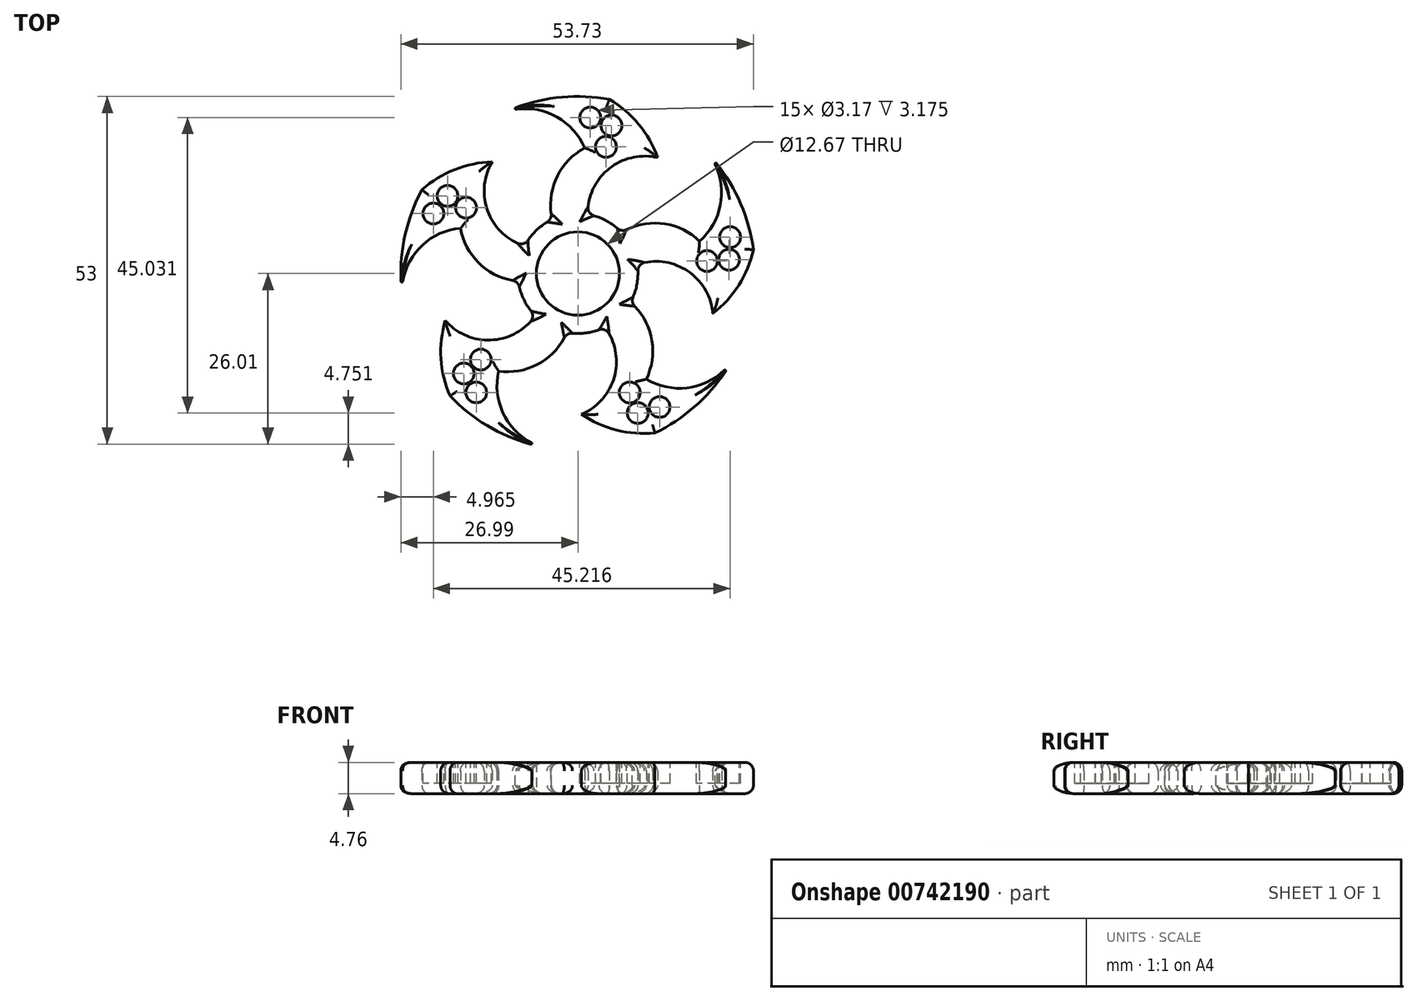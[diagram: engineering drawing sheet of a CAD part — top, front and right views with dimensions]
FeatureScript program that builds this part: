
annotation { "Feature Type Name" : "Feature", "Feature Type Description" : "" }
export const myFeature = defineFeature(function(context is Context, id is Id, definition is map)
    precondition{}
    {
        {
            var Q0;
            Q0=qCreatedBy(makeId("Top.planeOp"),FACE);
            var sketch = newSketch(context, id + "F0", { "sketchPlane" : qUnion([Q0])});
            skCircle(sketch, "E0", {"center": v(0, 0) * mm, "radius": 6.34 * mm});
            skArc(sketch, "E1", {"start": v(-9.07, -1.17) * mm, "mid": v(-8.22, -4) * mm, "end": v(-6.5, -6.43) * mm});
            skArc(sketch, "E2", {"start": v(-23.78, 12.77) * mm, "mid": v(-26.47, 5.28) * mm, "end": v(-26.86, -2.67) * mm});
            skArc(sketch, "E3", {"start": v(-17.89, 6.9) * mm, "mid": v(-24.2, 3.83) * mm, "end": v(-26.86, -2.67) * mm});
            skArc(sketch, "E4", {"start": v(-13.04, 17.02) * mm, "mid": v(-18.79, 15.84) * mm, "end": v(-23.78, 12.77) * mm});
            skArc(sketch, "E5", {"start": v(-17.89, 6.9) * mm, "mid": v(-14.85, 1.36) * mm, "end": v(-9.07, -1.17) * mm});
            skArc(sketch, "E6", {"start": v(-13.04, 17.02) * mm, "mid": v(-13.72, 9.4) * mm, "end": v(-8.12, 4.2) * mm});
            skArc(sketch, "E7.1.0", {"start": v(-20.22, -7.15) * mm, "mid": v(-20.87, -12.97) * mm, "end": v(-19.49, -18.67) * mm});
            skArc(sketch, "E7.1.1", {"start": v(-20.22, -7.15) * mm, "mid": v(-13.19, -10.14) * mm, "end": v(-6.5, -6.43) * mm});
            skArc(sketch, "E7.1.2", {"start": v(-12.09, -14.88) * mm, "mid": v(-5.89, -13.7) * mm, "end": v(-1.7, -8.99) * mm});
            skArc(sketch, "E7.1.3", {"start": v(-12.09, -14.88) * mm, "mid": v(-11.12, -21.83) * mm, "end": v(-5.76, -26.37) * mm});
            skArc(sketch, "E7.2.0", {"start": v(0.55, -21.44) * mm, "mid": v(5.89, -23.86) * mm, "end": v(11.73, -24.3) * mm});
            skArc(sketch, "E7.2.1", {"start": v(0.55, -21.44) * mm, "mid": v(5.57, -15.67) * mm, "end": v(4.1, -8.17) * mm});
            skArc(sketch, "E7.2.2", {"start": v(10.42, -16.1) * mm, "mid": v(11.21, -9.83) * mm, "end": v(8.02, -4.39) * mm});
            skArc(sketch, "E7.2.3", {"start": v(10.42, -16.1) * mm, "mid": v(17.33, -17.32) * mm, "end": v(23.3, -13.63) * mm});
            skArc(sketch, "E7.3.0", {"start": v(20.56, -6.1) * mm, "mid": v(24.5, -1.77) * mm, "end": v(26.74, 3.65) * mm});
            skArc(sketch, "E7.3.1", {"start": v(20.56, -6.1) * mm, "mid": v(16.63, 0.45) * mm, "end": v(9.04, 1.38) * mm});
            skArc(sketch, "E7.3.2", {"start": v(18.52, 4.93) * mm, "mid": v(12.82, 7.63) * mm, "end": v(6.65, 6.27) * mm});
            skArc(sketch, "E7.3.3", {"start": v(18.52, 4.93) * mm, "mid": v(21.83, 11.13) * mm, "end": v(20.16, 17.94) * mm});
            skArc(sketch, "E7.4.0", {"start": v(12.16, 17.67) * mm, "mid": v(9.26, 22.76) * mm, "end": v(4.8, 26.56) * mm});
            skArc(sketch, "E7.4.1", {"start": v(12.16, 17.67) * mm, "mid": v(4.71, 15.95) * mm, "end": v(1.49, 9.02) * mm});
            skArc(sketch, "E7.4.2", {"start": v(1.03, 19.14) * mm, "mid": v(-3.3, 14.55) * mm, "end": v(-3.91, 8.26) * mm});
            skArc(sketch, "E7.4.3", {"start": v(1.03, 19.14) * mm, "mid": v(-3.84, 24.2) * mm, "end": v(-10.84, 24.72) * mm});
            skArc(sketch, "E8.trimOffspring", {"start": v(4.8, 26.56) * mm, "mid": v(-3.16, 26.8) * mm, "end": v(-10.84, 24.72) * mm});
            skArc(sketch, "E9.trimOffspring", {"start": v(26.74, 3.65) * mm, "mid": v(24.51, 11.29) * mm, "end": v(20.16, 17.94) * mm});
            skArc(sketch, "E10.trimOffspring", {"start": v(11.73, -24.3) * mm, "mid": v(18.3, -19.83) * mm, "end": v(23.3, -13.63) * mm});
            skArc(sketch, "E11.trimOffspring", {"start": v(-19.49, -18.67) * mm, "mid": v(-13.2, -23.54) * mm, "end": v(-5.76, -26.37) * mm});
            skArc(sketch, "E12.trimOffspring", {"start": v(-1.7, -8.99) * mm, "mid": v(1.27, -9.06) * mm, "end": v(4.1, -8.17) * mm});
            skArc(sketch, "E13.trimOffspring", {"start": v(8.02, -4.39) * mm, "mid": v(9, -1.59) * mm, "end": v(9.04, 1.38) * mm});
            skArc(sketch, "E14.trimOffspring", {"start": v(6.65, 6.27) * mm, "mid": v(4.3, 8.07) * mm, "end": v(1.49, 9.02) * mm});
            skArc(sketch, "E15.trimOffspring", {"start": v(-3.91, 8.26) * mm, "mid": v(-6.35, 6.58) * mm, "end": v(-8.12, 4.2) * mm});
            skSolve(sketch);
        }
        {
            var Q0;
            Q0=qSketchRegion(id+"F0",true);
            extrude(context, id + "F1", {"entities" : qUnion([Q0]), "depth" : 4.76 * mm, "offsetDistance" : 25.4 * mm});
        }
        {
            var Q0;
            Q0=makeQuery(id+"F1.opExtrude","CAP_EDGE",EDGE,{"disambiguationData":[OSD([sQuery(id+"F0.wireOp",EDGE,"E5")])],"isStart":false});
            var Q1;
            Q1=makeQuery(id+"F1.opExtrude","CAP_EDGE",EDGE,{"disambiguationData":[OSD([sQuery(id+"F0.wireOp",EDGE,"E3")])],"isStart":false});
            var Q2;
            Q2=makeQuery(id+"F1.opExtrude","CAP_EDGE",EDGE,{"disambiguationData":[OSD([sQuery(id+"F0.wireOp",EDGE,"E2")])],"isStart":false});
            var Q3;
            Q3=makeQuery(id+"F1.opExtrude","CAP_EDGE",EDGE,{"disambiguationData":[OSD([sQuery(id+"F0.wireOp",EDGE,"E4")])],"isStart":false});
            var Q4;
            Q4=makeQuery(id+"F1.opExtrude","CAP_EDGE",EDGE,{"disambiguationData":[OSD([sQuery(id+"F0.wireOp",EDGE,"E6")])],"isStart":false});
            var Q5;
            Q5=makeQuery(id+"F1.opExtrude","CAP_EDGE",EDGE,{"disambiguationData":[OSD([sQuery(id+"F0.wireOp",EDGE,"E15.trimOffspring")])],"isStart":false});
            var Q6;
            Q6=makeQuery(id+"F1.opExtrude","CAP_EDGE",EDGE,{"disambiguationData":[OSD([sQuery(id+"F0.wireOp",EDGE,"E7.4.2")])],"isStart":false});
            var Q7;
            Q7=makeQuery(id+"F1.opExtrude","CAP_EDGE",EDGE,{"disambiguationData":[OSD([sQuery(id+"F0.wireOp",EDGE,"E7.4.3")])],"isStart":false});
            var Q8;
            Q8=makeQuery(id+"F1.opExtrude","CAP_EDGE",EDGE,{"disambiguationData":[OSD([sQuery(id+"F0.wireOp",EDGE,"E8.trimOffspring")])],"isStart":false});
            var Q9;
            Q9=makeQuery(id+"F1.opExtrude","CAP_EDGE",EDGE,{"disambiguationData":[OSD([sQuery(id+"F0.wireOp",EDGE,"E7.4.0")])],"isStart":false});
            var Q10;
            Q10=makeQuery(id+"F1.opExtrude","CAP_EDGE",EDGE,{"disambiguationData":[OSD([sQuery(id+"F0.wireOp",EDGE,"E7.4.1")])],"isStart":false});
            var Q11;
            Q11=makeQuery(id+"F1.opExtrude","CAP_EDGE",EDGE,{"disambiguationData":[OSD([sQuery(id+"F0.wireOp",EDGE,"E14.trimOffspring")])],"isStart":false});
            var Q12;
            Q12=makeQuery(id+"F1.opExtrude","CAP_EDGE",EDGE,{"disambiguationData":[OSD([sQuery(id+"F0.wireOp",EDGE,"E7.3.2")])],"isStart":false});
            var Q13;
            Q13=makeQuery(id+"F1.opExtrude","CAP_EDGE",EDGE,{"disambiguationData":[OSD([sQuery(id+"F0.wireOp",EDGE,"E7.3.3")])],"isStart":false});
            var Q14;
            Q14=makeQuery(id+"F1.opExtrude","CAP_EDGE",EDGE,{"disambiguationData":[OSD([sQuery(id+"F0.wireOp",EDGE,"E9.trimOffspring")])],"isStart":false});
            var Q15;
            Q15=makeQuery(id+"F1.opExtrude","CAP_EDGE",EDGE,{"disambiguationData":[OSD([sQuery(id+"F0.wireOp",EDGE,"E7.3.0")])],"isStart":false});
            var Q16;
            Q16=makeQuery(id+"F1.opExtrude","CAP_EDGE",EDGE,{"disambiguationData":[OSD([sQuery(id+"F0.wireOp",EDGE,"E7.3.1")])],"isStart":false});
            var Q17;
            Q17=makeQuery(id+"F1.opExtrude","CAP_EDGE",EDGE,{"disambiguationData":[OSD([sQuery(id+"F0.wireOp",EDGE,"E13.trimOffspring")])],"isStart":false});
            var Q18;
            Q18=makeQuery(id+"F1.opExtrude","CAP_EDGE",EDGE,{"disambiguationData":[OSD([sQuery(id+"F0.wireOp",EDGE,"E7.2.2")])],"isStart":false});
            var Q19;
            Q19=makeQuery(id+"F1.opExtrude","CAP_EDGE",EDGE,{"disambiguationData":[OSD([sQuery(id+"F0.wireOp",EDGE,"E7.2.3")])],"isStart":false});
            var Q20;
            Q20=makeQuery(id+"F1.opExtrude","CAP_EDGE",EDGE,{"disambiguationData":[OSD([sQuery(id+"F0.wireOp",EDGE,"E10.trimOffspring")])],"isStart":false});
            var Q21;
            Q21=makeQuery(id+"F1.opExtrude","CAP_EDGE",EDGE,{"disambiguationData":[OSD([sQuery(id+"F0.wireOp",EDGE,"E7.2.0")])],"isStart":false});
            var Q22;
            Q22=makeQuery(id+"F1.opExtrude","CAP_EDGE",EDGE,{"disambiguationData":[OSD([sQuery(id+"F0.wireOp",EDGE,"E7.2.1")])],"isStart":false});
            var Q23;
            Q23=makeQuery(id+"F1.opExtrude","CAP_EDGE",EDGE,{"disambiguationData":[OSD([sQuery(id+"F0.wireOp",EDGE,"E12.trimOffspring")])],"isStart":false});
            var Q24;
            Q24=makeQuery(id+"F1.opExtrude","CAP_EDGE",EDGE,{"disambiguationData":[OSD([sQuery(id+"F0.wireOp",EDGE,"E7.1.2")])],"isStart":false});
            var Q25;
            Q25=makeQuery(id+"F1.opExtrude","CAP_EDGE",EDGE,{"disambiguationData":[OSD([sQuery(id+"F0.wireOp",EDGE,"E7.1.3")])],"isStart":false});
            var Q26;
            Q26=makeQuery(id+"F1.opExtrude","CAP_EDGE",EDGE,{"disambiguationData":[OSD([sQuery(id+"F0.wireOp",EDGE,"E11.trimOffspring")])],"isStart":false});
            var Q27;
            Q27=makeQuery(id+"F1.opExtrude","CAP_EDGE",EDGE,{"disambiguationData":[OSD([sQuery(id+"F0.wireOp",EDGE,"E7.1.0")])],"isStart":false});
            var Q28;
            Q28=makeQuery(id+"F1.opExtrude","CAP_EDGE",EDGE,{"disambiguationData":[OSD([sQuery(id+"F0.wireOp",EDGE,"E7.1.1")])],"isStart":false});
            var Q29;
            Q29=makeQuery(id+"F1.opExtrude","CAP_EDGE",EDGE,{"disambiguationData":[OSD([sQuery(id+"F0.wireOp",EDGE,"E1")])],"isStart":false});
            var Q30;
            Q30=makeQuery(id+"F1.opExtrude","CAP_EDGE",EDGE,{"disambiguationData":[OSD([sQuery(id+"F0.wireOp",EDGE,"E7.1.0")])],"isStart":true});
            var Q31;
            Q31=makeQuery(id+"F1.opExtrude","CAP_EDGE",EDGE,{"disambiguationData":[OSD([sQuery(id+"F0.wireOp",EDGE,"E11.trimOffspring")])],"isStart":true});
            var Q32;
            Q32=makeQuery(id+"F1.opExtrude","CAP_EDGE",EDGE,{"disambiguationData":[OSD([sQuery(id+"F0.wireOp",EDGE,"E7.1.3")])],"isStart":true});
            var Q33;
            Q33=makeQuery(id+"F1.opExtrude","CAP_EDGE",EDGE,{"disambiguationData":[OSD([sQuery(id+"F0.wireOp",EDGE,"E7.1.2")])],"isStart":true});
            var Q34;
            Q34=makeQuery(id+"F1.opExtrude","CAP_EDGE",EDGE,{"disambiguationData":[OSD([sQuery(id+"F0.wireOp",EDGE,"E12.trimOffspring")])],"isStart":true});
            var Q35;
            Q35=makeQuery(id+"F1.opExtrude","CAP_EDGE",EDGE,{"disambiguationData":[OSD([sQuery(id+"F0.wireOp",EDGE,"E7.2.1")])],"isStart":true});
            var Q36;
            Q36=makeQuery(id+"F1.opExtrude","CAP_EDGE",EDGE,{"disambiguationData":[OSD([sQuery(id+"F0.wireOp",EDGE,"E7.2.0")])],"isStart":true});
            var Q37;
            Q37=makeQuery(id+"F1.opExtrude","CAP_EDGE",EDGE,{"disambiguationData":[OSD([sQuery(id+"F0.wireOp",EDGE,"E10.trimOffspring")])],"isStart":true});
            var Q38;
            Q38=makeQuery(id+"F1.opExtrude","CAP_EDGE",EDGE,{"disambiguationData":[OSD([sQuery(id+"F0.wireOp",EDGE,"E7.2.3")])],"isStart":true});
            var Q39;
            Q39=makeQuery(id+"F1.opExtrude","CAP_EDGE",EDGE,{"disambiguationData":[OSD([sQuery(id+"F0.wireOp",EDGE,"E7.2.2")])],"isStart":true});
            var Q40;
            Q40=makeQuery(id+"F1.opExtrude","CAP_EDGE",EDGE,{"disambiguationData":[OSD([sQuery(id+"F0.wireOp",EDGE,"E13.trimOffspring")])],"isStart":true});
            var Q41;
            Q41=makeQuery(id+"F1.opExtrude","CAP_EDGE",EDGE,{"disambiguationData":[OSD([sQuery(id+"F0.wireOp",EDGE,"E7.3.1")])],"isStart":true});
            var Q42;
            Q42=makeQuery(id+"F1.opExtrude","CAP_EDGE",EDGE,{"disambiguationData":[OSD([sQuery(id+"F0.wireOp",EDGE,"E7.3.0")])],"isStart":true});
            var Q43;
            Q43=makeQuery(id+"F1.opExtrude","CAP_EDGE",EDGE,{"disambiguationData":[OSD([sQuery(id+"F0.wireOp",EDGE,"E9.trimOffspring")])],"isStart":true});
            var Q44;
            Q44=makeQuery(id+"F1.opExtrude","CAP_EDGE",EDGE,{"disambiguationData":[OSD([sQuery(id+"F0.wireOp",EDGE,"E7.3.3")])],"isStart":true});
            var Q45;
            Q45=makeQuery(id+"F1.opExtrude","CAP_EDGE",EDGE,{"disambiguationData":[OSD([sQuery(id+"F0.wireOp",EDGE,"E7.3.2")])],"isStart":true});
            var Q46;
            Q46=makeQuery(id+"F1.opExtrude","CAP_EDGE",EDGE,{"disambiguationData":[OSD([sQuery(id+"F0.wireOp",EDGE,"E14.trimOffspring")])],"isStart":true});
            var Q47;
            Q47=makeQuery(id+"F1.opExtrude","CAP_EDGE",EDGE,{"disambiguationData":[OSD([sQuery(id+"F0.wireOp",EDGE,"E7.4.1")])],"isStart":true});
            var Q48;
            Q48=makeQuery(id+"F1.opExtrude","CAP_EDGE",EDGE,{"disambiguationData":[OSD([sQuery(id+"F0.wireOp",EDGE,"E7.4.0")])],"isStart":true});
            var Q49;
            Q49=makeQuery(id+"F1.opExtrude","CAP_EDGE",EDGE,{"disambiguationData":[OSD([sQuery(id+"F0.wireOp",EDGE,"E7.1.1")])],"isStart":true});
            var Q50;
            Q50=makeQuery(id+"F1.opExtrude","CAP_EDGE",EDGE,{"disambiguationData":[OSD([sQuery(id+"F0.wireOp",EDGE,"E1")])],"isStart":true});
            var Q51;
            Q51=makeQuery(id+"F1.opExtrude","CAP_EDGE",EDGE,{"disambiguationData":[OSD([sQuery(id+"F0.wireOp",EDGE,"E5")])],"isStart":true});
            var Q52;
            Q52=makeQuery(id+"F1.opExtrude","CAP_EDGE",EDGE,{"disambiguationData":[OSD([sQuery(id+"F0.wireOp",EDGE,"E3")])],"isStart":true});
            var Q53;
            Q53=makeQuery(id+"F1.opExtrude","CAP_EDGE",EDGE,{"disambiguationData":[OSD([sQuery(id+"F0.wireOp",EDGE,"E2")])],"isStart":true});
            var Q54;
            Q54=makeQuery(id+"F1.opExtrude","CAP_EDGE",EDGE,{"disambiguationData":[OSD([sQuery(id+"F0.wireOp",EDGE,"E4")])],"isStart":true});
            var Q55;
            Q55=makeQuery(id+"F1.opExtrude","CAP_EDGE",EDGE,{"disambiguationData":[OSD([sQuery(id+"F0.wireOp",EDGE,"E6")])],"isStart":true});
            var Q56;
            Q56=makeQuery(id+"F1.opExtrude","CAP_EDGE",EDGE,{"disambiguationData":[OSD([sQuery(id+"F0.wireOp",EDGE,"E15.trimOffspring")])],"isStart":true});
            var Q57;
            Q57=makeQuery(id+"F1.opExtrude","CAP_EDGE",EDGE,{"disambiguationData":[OSD([sQuery(id+"F0.wireOp",EDGE,"E7.4.2")])],"isStart":true});
            var Q58;
            Q58=makeQuery(id+"F1.opExtrude","CAP_EDGE",EDGE,{"disambiguationData":[OSD([sQuery(id+"F0.wireOp",EDGE,"E7.4.3")])],"isStart":true});
            var Q59;
            Q59=makeQuery(id+"F1.opExtrude","CAP_EDGE",EDGE,{"disambiguationData":[OSD([sQuery(id+"F0.wireOp",EDGE,"E8.trimOffspring")])],"isStart":true});
            fillet(context, id + "F2", {"entities" : qUnion([Q0, Q1, Q2, Q3, Q4, Q5, Q6, Q7, Q8, Q9, Q10, Q11, Q12, Q13, Q14, Q15, Q16, Q17, Q18, Q19, Q20, Q21, Q22, Q23, Q24, Q25, Q26, Q27, Q28, Q29, Q30, Q31, Q32, Q33, Q34, Q35, Q36, Q37, Q38, Q39, Q40, Q41, Q42, Q43, Q44, Q45, Q46, Q47, Q48, Q49, Q50, Q51, Q52, Q53, Q54, Q55, Q56, Q57, Q58, Q59]), "radius" : 1.27 * mm, "tangentPropagation" : true, "allowEdgeOverflow" : false});
        }
        {
            var Q0;
            Q0=makeQuery(id+"F1.opExtrude","SWEPT_EDGE",EDGE,{"disambiguationData":[OSD([sQuery(id+"F0.wireOp",EDGE,"E6"),sQuery(id+"F0.wireOp",EDGE,"E15.trimOffspring")])]});
            var Q1;
            Q1=makeQuery(id+"F1.opExtrude","SWEPT_EDGE",EDGE,{"disambiguationData":[OSD([sQuery(id+"F0.wireOp",EDGE,"E7.4.2"),sQuery(id+"F0.wireOp",EDGE,"E15.trimOffspring")])]});
            var Q2;
            Q2=makeQuery(id+"F1.opExtrude","SWEPT_EDGE",EDGE,{"disambiguationData":[OSD([sQuery(id+"F0.wireOp",EDGE,"E1"),sQuery(id+"F0.wireOp",EDGE,"E7.1.1")])]});
            var Q3;
            Q3=makeQuery(id+"F1.opExtrude","SWEPT_EDGE",EDGE,{"disambiguationData":[OSD([sQuery(id+"F0.wireOp",EDGE,"E1"),sQuery(id+"F0.wireOp",EDGE,"E5")])]});
            var Q4;
            Q4=makeQuery(id+"F1.opExtrude","SWEPT_EDGE",EDGE,{"disambiguationData":[OSD([sQuery(id+"F0.wireOp",EDGE,"E7.4.1"),sQuery(id+"F0.wireOp",EDGE,"E14.trimOffspring")])]});
            var Q5;
            Q5=makeQuery(id+"F1.opExtrude","SWEPT_EDGE",EDGE,{"disambiguationData":[OSD([sQuery(id+"F0.wireOp",EDGE,"E7.2.2"),sQuery(id+"F0.wireOp",EDGE,"E13.trimOffspring")])]});
            var Q6;
            Q6=makeQuery(id+"F1.opExtrude","SWEPT_EDGE",EDGE,{"disambiguationData":[OSD([sQuery(id+"F0.wireOp",EDGE,"E7.3.1"),sQuery(id+"F0.wireOp",EDGE,"E13.trimOffspring")])]});
            var Q7;
            Q7=makeQuery(id+"F1.opExtrude","SWEPT_EDGE",EDGE,{"disambiguationData":[OSD([sQuery(id+"F0.wireOp",EDGE,"E7.3.2"),sQuery(id+"F0.wireOp",EDGE,"E14.trimOffspring")])]});
            var Q8;
            Q8=makeQuery(id+"F1.opExtrude","SWEPT_EDGE",EDGE,{"disambiguationData":[OSD([sQuery(id+"F0.wireOp",EDGE,"E7.1.2"),sQuery(id+"F0.wireOp",EDGE,"E12.trimOffspring")])]});
            var Q9;
            Q9=makeQuery(id+"F1.opExtrude","SWEPT_EDGE",EDGE,{"disambiguationData":[OSD([sQuery(id+"F0.wireOp",EDGE,"E7.2.1"),sQuery(id+"F0.wireOp",EDGE,"E12.trimOffspring")])]});
            fillet(context, id + "F3", {"entities" : qUnion([Q0, Q1, Q2, Q3, Q4, Q5, Q6, Q7, Q8, Q9]), "radius" : 1.27 * mm, "tangentPropagation" : true, "allowEdgeOverflow" : false});
        }
        {
            var Q0;
            Q0=makeQuery(id+"F1.opExtrude","SWEPT_EDGE",EDGE,{"disambiguationData":[OSD([sQuery(id+"F0.wireOp",EDGE,"E7.4.3"),sQuery(id+"F0.wireOp",EDGE,"E8.trimOffspring")])]});
            var Q1;
            Q1=makeQuery(id+"F1.opExtrude","SWEPT_EDGE",EDGE,{"disambiguationData":[OSD([sQuery(id+"F0.wireOp",EDGE,"E2"),sQuery(id+"F0.wireOp",EDGE,"E3")])]});
            var Q2;
            Q2=makeQuery(id+"F1.opExtrude","SWEPT_EDGE",EDGE,{"disambiguationData":[OSD([sQuery(id+"F0.wireOp",EDGE,"E7.1.3"),sQuery(id+"F0.wireOp",EDGE,"E11.trimOffspring")])]});
            var Q3;
            Q3=makeQuery(id+"F1.opExtrude","SWEPT_EDGE",EDGE,{"disambiguationData":[OSD([sQuery(id+"F0.wireOp",EDGE,"E7.2.3"),sQuery(id+"F0.wireOp",EDGE,"E10.trimOffspring")])]});
            var Q4;
            Q4=makeQuery(id+"F1.opExtrude","SWEPT_EDGE",EDGE,{"disambiguationData":[OSD([sQuery(id+"F0.wireOp",EDGE,"E7.3.3"),sQuery(id+"F0.wireOp",EDGE,"E9.trimOffspring")])]});
            fillet(context, id + "F4", {"entities" : qUnion([Q0, Q1, Q2, Q3, Q4]), "radius" : 0.13 * mm, "tangentPropagation" : true, "allowEdgeOverflow" : false});
        }
        {
            var Q0;
            Q0=makeQuery(id+"F1.opExtrude","CAP_FACE",FACE,{"disambiguationData":[OSD([sQuery(id+"F0.wireOp",EDGE,"E0"),sQuery(id+"F0.wireOp",EDGE,"E1"),sQuery(id+"F0.wireOp",EDGE,"E2"),sQuery(id+"F0.wireOp",EDGE,"E3"),sQuery(id+"F0.wireOp",EDGE,"E4"),sQuery(id+"F0.wireOp",EDGE,"E5"),sQuery(id+"F0.wireOp",EDGE,"E6"),sQuery(id+"F0.wireOp",EDGE,"E7.1.0"),sQuery(id+"F0.wireOp",EDGE,"E7.1.1"),sQuery(id+"F0.wireOp",EDGE,"E7.1.2"),sQuery(id+"F0.wireOp",EDGE,"E7.1.3"),sQuery(id+"F0.wireOp",EDGE,"E7.2.0"),sQuery(id+"F0.wireOp",EDGE,"E7.2.1"),sQuery(id+"F0.wireOp",EDGE,"E7.2.2"),sQuery(id+"F0.wireOp",EDGE,"E7.2.3"),sQuery(id+"F0.wireOp",EDGE,"E7.3.0"),sQuery(id+"F0.wireOp",EDGE,"E7.3.1"),sQuery(id+"F0.wireOp",EDGE,"E7.3.2"),sQuery(id+"F0.wireOp",EDGE,"E7.3.3"),sQuery(id+"F0.wireOp",EDGE,"E7.4.0"),sQuery(id+"F0.wireOp",EDGE,"E7.4.1"),sQuery(id+"F0.wireOp",EDGE,"E7.4.2"),sQuery(id+"F0.wireOp",EDGE,"E7.4.3"),sQuery(id+"F0.wireOp",EDGE,"E8.trimOffspring"),sQuery(id+"F0.wireOp",EDGE,"E9.trimOffspring"),sQuery(id+"F0.wireOp",EDGE,"E10.trimOffspring"),sQuery(id+"F0.wireOp",EDGE,"E11.trimOffspring"),sQuery(id+"F0.wireOp",EDGE,"E12.trimOffspring"),sQuery(id+"F0.wireOp",EDGE,"E13.trimOffspring"),sQuery(id+"F0.wireOp",EDGE,"E14.trimOffspring"),sQuery(id+"F0.wireOp",EDGE,"E15.trimOffspring")])],"isStart":false});
            var sketch = newSketch(context, id + "F5", { "sketchPlane" : qUnion([Q0])});
            skCircle(sketch, "E16", {"center": v(1.89, 23.77) * mm, "radius": 1.59 * mm});
            skCircle(sketch, "E17", {"center": v(5.12, 22.56) * mm, "radius": 1.59 * mm});
            skCircle(sketch, "E18", {"center": v(4.27, 19.3) * mm, "radius": 1.59 * mm});
            skCircle(sketch, "E19.1.0", {"center": v(-22.03, 9.14) * mm, "radius": 1.59 * mm});
            skCircle(sketch, "E19.1.1", {"center": v(-19.87, 11.84) * mm, "radius": 1.59 * mm});
            skCircle(sketch, "E19.1.2", {"center": v(-17.04, 10.03) * mm, "radius": 1.59 * mm});
            skCircle(sketch, "E19.2.0", {"center": v(-15.5, -18.12) * mm, "radius": 1.59 * mm});
            skCircle(sketch, "E19.2.1", {"center": v(-17.4, -15.24) * mm, "radius": 1.59 * mm});
            skCircle(sketch, "E19.2.2", {"center": v(-14.8, -13.1) * mm, "radius": 1.59 * mm});
            skCircle(sketch, "E19.3.0", {"center": v(12.45, -20.34) * mm, "radius": 1.59 * mm});
            skCircle(sketch, "E19.3.1", {"center": v(9.12, -21.26) * mm, "radius": 1.59 * mm});
            skCircle(sketch, "E19.3.2", {"center": v(7.9, -18.13) * mm, "radius": 1.59 * mm});
            skCircle(sketch, "E19.4.0", {"center": v(23.2, 5.55) * mm, "radius": 1.59 * mm});
            skCircle(sketch, "E19.4.1", {"center": v(23.04, 2.1) * mm, "radius": 1.59 * mm});
            skCircle(sketch, "E19.4.2", {"center": v(19.68, 1.9) * mm, "radius": 1.59 * mm});
            skPoint(sketch, "E19.center", {"position": v(0, 0) * mm});
            skSolve(sketch);
        }
        {
            var Q0;
            Q0=qSketchRegion(id+"F5",true);
            extrude(context, id + "F6", {"entities" : qUnion([Q0]), "operationType" : NewBodyOperationType.REMOVE, "oppositeDirection" : true, "depth" : 3.17 * mm, "offsetDistance" : 25.4 * mm});
        }
    });
